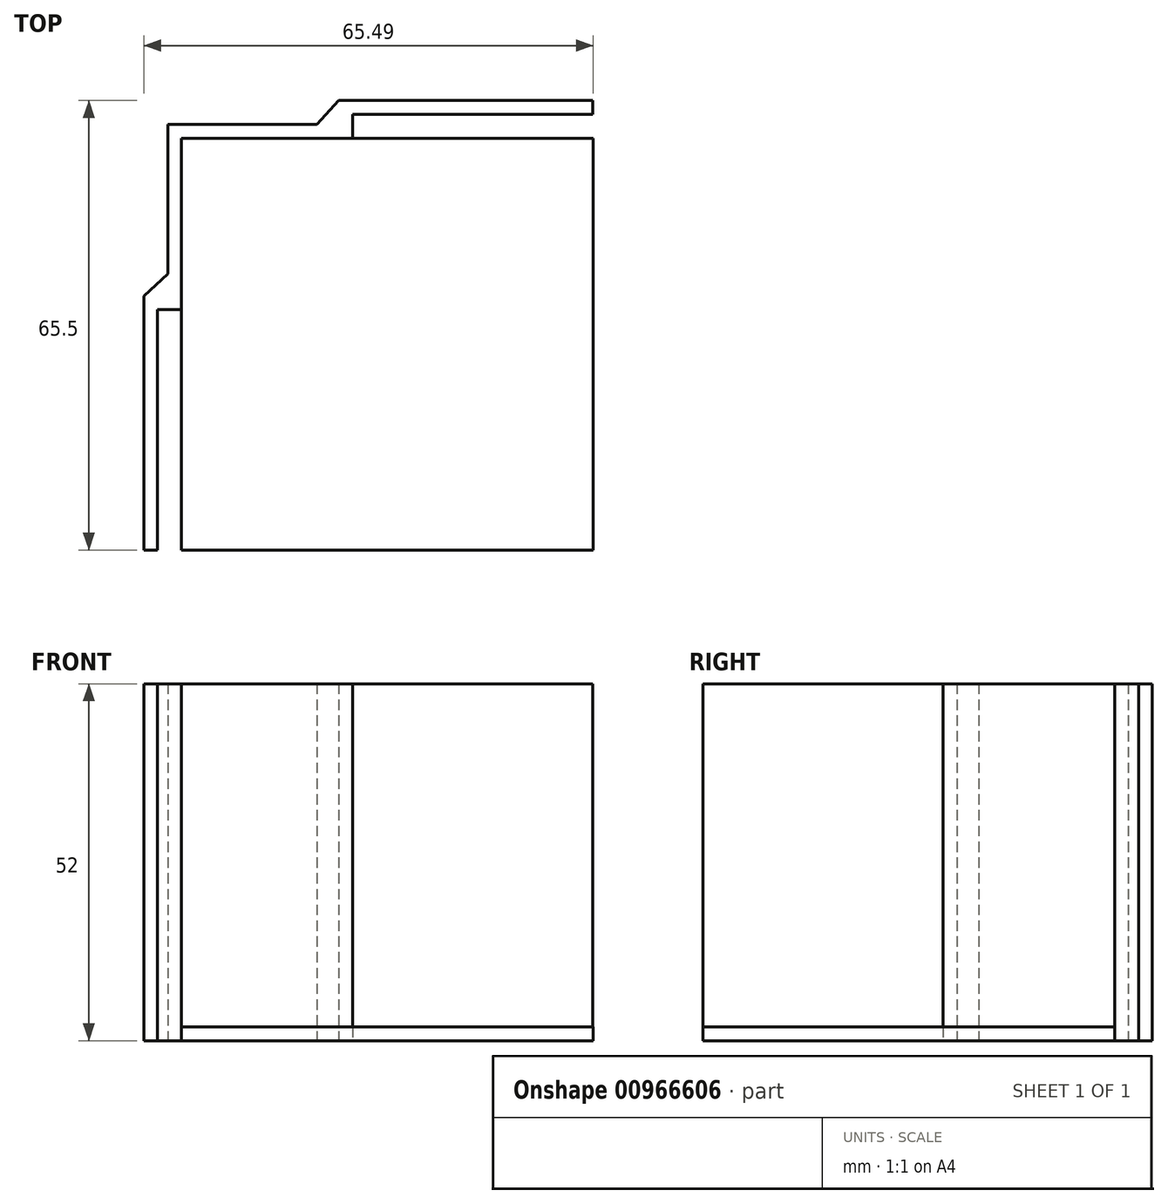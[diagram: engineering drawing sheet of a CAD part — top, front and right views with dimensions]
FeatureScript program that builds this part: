
annotation { "Feature Type Name" : "Feature", "Feature Type Description" : "" }
export const myFeature = defineFeature(function(context is Context, id is Id, definition is map)
    precondition{}
    {
        {
            var Q0;
            Q0=qCreatedBy(makeId("Top.planeOp"),FACE);
            var sketch = newSketch(context, id + "F0", { "sketchPlane" : qUnion([Q0])});
            skLineSegment(sketch, "E0.bottom", {"start": v(-29.86, 30.18) * mm, "end": v(30.14, 30.18) * mm});
            skLineSegment(sketch, "E0.top", {"start": v(-29.86, -29.82) * mm, "end": v(30.14, -29.82) * mm});
            skLineSegment(sketch, "E0.left", {"start": v(-29.86, 30.18) * mm, "end": v(-29.86, -29.82) * mm});
            skLineSegment(sketch, "E0.right", {"start": v(30.14, 30.18) * mm, "end": v(30.14, -29.82) * mm});
            skLineSegment(sketch, "E1", {"start": v(-29.86, 0.18) * mm, "end": v(30.14, 0.18) * mm});
            skLineSegment(sketch, "E2", {"start": v(0.14, 30.18) * mm, "end": v(0.14, -29.82) * mm});
            skLineSegment(sketch, "E3", {"start": v(-29.86, 30.18) * mm, "end": v(-29.86, 5.18) * mm});
            skLineSegment(sketch, "E4", {"start": v(-29.85, 5.18) * mm, "end": v(-33.35, 5.18) * mm});
            skLineSegment(sketch, "E5", {"start": v(-29.85, -29.82) * mm, "end": v(-33.35, -29.82) * mm});
            skLineSegment(sketch, "E6", {"start": v(-33.35, 5.18) * mm, "end": v(-33.35, -29.82) * mm});
            skLineSegment(sketch, "E7.1", {"start": v(-35.35, 7.18) * mm, "end": v(-35.35, -29.82) * mm});
            skLineSegment(sketch, "E7.2", {"start": v(-29.85, 7.18) * mm, "end": v(-35.35, 7.18) * mm});
            skLineSegment(sketch, "E8", {"start": v(-33.35, -29.82) * mm, "end": v(-35.35, -29.82) * mm});
            skLineSegment(sketch, "E9", {"start": v(-29.86, 30.18) * mm, "end": v(-4.86, 30.18) * mm});
            skLineSegment(sketch, "E10.MirrorCS", {"start": v(30.1, 30.18) * mm, "end": v(30.1, 33.68) * mm});
            skLineSegment(sketch, "E11.MirrorCS", {"start": v(-6.9, 30.18) * mm, "end": v(-6.9, 35.68) * mm});
            skLineSegment(sketch, "E12.MirrorCS", {"start": v(-6.9, 35.68) * mm, "end": v(30.1, 35.68) * mm});
            skLineSegment(sketch, "E13.MirrorCS", {"start": v(-4.9, 30.18) * mm, "end": v(-4.9, 33.68) * mm});
            skLineSegment(sketch, "E14.MirrorCS", {"start": v(-4.9, 33.68) * mm, "end": v(30.1, 33.68) * mm});
            skLineSegment(sketch, "E15.MirrorCS", {"start": v(30.1, 33.68) * mm, "end": v(30.1, 35.68) * mm});
            skLineSegment(sketch, "E16", {"start": v(-6.9, 30.18) * mm, "end": v(-11.93, 30.18) * mm});
            skLineSegment(sketch, "E17", {"start": v(-11.93, 30.18) * mm, "end": v(-6.9, 35.68) * mm});
            skLineSegment(sketch, "E18", {"start": v(-35.35, 7.18) * mm, "end": v(-29.86, 12.26) * mm});
            skLineSegment(sketch, "E19.0", {"start": v(-31.86, 32.18) * mm, "end": v(-4.86, 32.18) * mm});
            skLineSegment(sketch, "E19.1", {"start": v(-31.86, 32.18) * mm, "end": v(-31.86, 5.18) * mm});
            skSolve(sketch);
        }
        {
            var Q0;
            {var subQ0=sQuery(id+"F0.wireOp",EDGE,"E2");var subQ5=sQuery(id+"F0.wireOp",EDGE,"E0.bottom");var subQ8=makeQuery(id+"F0.imprint","INTERSECT",VERTEX,{"derivedFrom":[subQ5,subQ0]});Q0=makeQuery(id+"F0.imprint","IMPRINT",FACE,{"disambiguationData":[TD([[makeQuery(id+"F0.imprint","IMPRINT",EDGE,{"disambiguationData":[TD([[subQ8,-1.0]])],"derivedFrom":subQ5}),-1.0]])]});}
            var Q1;
            {var subQ0=sQuery(id+"F0.wireOp",EDGE,"E2");var subQ1=sQuery(id+"F0.wireOp",EDGE,"E0.top");var subQ2=makeQuery(id+"F0.imprint","INTERSECT",VERTEX,{"derivedFrom":[subQ1,subQ0]});Q1=makeQuery(id+"F0.imprint","IMPRINT",FACE,{"disambiguationData":[TD([[makeQuery(id+"F0.imprint","IMPRINT",EDGE,{"disambiguationData":[TD([[subQ2,-1.0]])],"derivedFrom":subQ1}),1.0]])]});}
            var Q2;
            {var subQ3=sQuery(id+"F0.wireOp",EDGE,"E0.top");var subQ5=makeQuery(id+"F0.imprint","IMPRINT",VERTEX,{"derivedFrom":subQ3});Q2=makeQuery(id+"F0.imprint","IMPRINT",FACE,{"disambiguationData":[TD([[makeQuery(id+"F0.imprint","IMPRINT",EDGE,{"disambiguationData":[TD([[subQ5,-1.0]])],"derivedFrom":subQ3}),1.0]])]});}
            var Q3;
            {var subQ6=sQuery(id+"F0.wireOp",EDGE,"E0.bottom");var subQ9=makeQuery(id+"F0.imprint","IMPRINT",VERTEX,{"derivedFrom":subQ6});Q3=makeQuery(id+"F0.imprint","IMPRINT",FACE,{"disambiguationData":[TD([[makeQuery(id+"F0.imprint","IMPRINT",EDGE,{"disambiguationData":[TD([[subQ9,-1.0]])],"derivedFrom":subQ6}),-1.0]])]});}
            extrude(context, id + "F1", {"entities" : qUnion([Q0, Q1, Q2, Q3]), "depth" : 2 * mm, "offsetDistance" : 25 * mm});
        }
        {
            var Q0;
            {var subQ4=sQuery(id+"F0.wireOp",EDGE,"E6");Q0=makeQuery(id+"F0.imprint","IMPRINT",FACE,{"disambiguationData":[TD([[makeQuery(id+"F0.imprint","IMPRINT",EDGE,{"derivedFrom":subQ4}),-1.0]])]});}
            var Q1;
            {var subQ0=sQuery(id+"F0.wireOp",EDGE,"E13.MirrorCS");var subQ1=sQuery(id+"F0.wireOp",EDGE,"E0.bottom");var subQ2=makeQuery(id+"F0.imprint","INTERSECT",VERTEX,{"derivedFrom":[subQ1,subQ0]});Q1=makeQuery(id+"F0.imprint","IMPRINT",FACE,{"disambiguationData":[TD([[makeQuery(id+"F0.imprint","IMPRINT",EDGE,{"disambiguationData":[TD([[subQ2,1.0]])],"derivedFrom":subQ1}),1.0]])]});}
            var Q2;
            {var subQ0=sQuery(id+"F0.wireOp",EDGE,"E19.0");var subQ1=sQuery(id+"F0.wireOp",EDGE,"E11.MirrorCS");var subQ2=makeQuery(id+"F0.imprint","INTERSECT",VERTEX,{"derivedFrom":[subQ1,subQ0]});Q2=makeQuery(id+"F0.imprint","IMPRINT",FACE,{"disambiguationData":[TD([[makeQuery(id+"F0.imprint","IMPRINT",EDGE,{"disambiguationData":[TD([[subQ2,1.0]])],"derivedFrom":subQ0}),1.0]])]});}
            var Q3;
            {var subQ1=sQuery(id+"F0.wireOp",EDGE,"E7.2");var subQ3=sQuery(id+"F0.wireOp",EDGE,"E19.1");var subQ4=makeQuery(id+"F0.imprint","INTERSECT",VERTEX,{"derivedFrom":[subQ1,subQ3]});Q3=makeQuery(id+"F0.imprint","IMPRINT",FACE,{"disambiguationData":[TD([[makeQuery(id+"F0.imprint","IMPRINT",EDGE,{"disambiguationData":[TD([[subQ4,1.0]])],"derivedFrom":subQ3}),-1.0]])]});}
            var Q4;
            {var subQ0=sQuery(id+"F0.wireOp",EDGE,"E17");var subQ1=sQuery(id+"F0.wireOp",EDGE,"E0.bottom");var subQ2=makeQuery(id+"F0.imprint","INTERSECT",VERTEX,{"derivedFrom":[subQ1,subQ0]});Q4=makeQuery(id+"F0.imprint","IMPRINT",FACE,{"disambiguationData":[TD([[makeQuery(id+"F0.imprint","IMPRINT",EDGE,{"disambiguationData":[TD([[subQ2,-1.0]])],"derivedFrom":subQ1}),1.0]])]});}
            var Q5;
            {var subQ4=sQuery(id+"F0.wireOp",EDGE,"E12.MirrorCS");Q5=makeQuery(id+"F0.imprint","IMPRINT",FACE,{"disambiguationData":[TD([[makeQuery(id+"F0.imprint","IMPRINT",EDGE,{"derivedFrom":subQ4}),-1.0]])]});}
            var Q6;
            {var subQ1=sQuery(id+"F0.wireOp",EDGE,"E0.left");var subQ8=sQuery(id+"F0.wireOp",EDGE,"E0.bottom");var subQ10=makeQuery(id+"F0.imprint","INTERSECT",VERTEX,{"derivedFrom":[subQ8,subQ1]});Q6=makeQuery(id+"F0.imprint","IMPRINT",FACE,{"disambiguationData":[TD([[makeQuery(id+"F0.imprint","IMPRINT",EDGE,{"disambiguationData":[TD([[subQ10,-1.0]])],"derivedFrom":subQ8}),1.0]])]});}
            var Q7;
            {var subQ0=sQuery(id+"F0.wireOp",EDGE,"E7.2");var subQ1=sQuery(id+"F0.wireOp",EDGE,"E0.left");var subQ2=makeQuery(id+"F0.imprint","INTERSECT",VERTEX,{"derivedFrom":[subQ1,subQ0]});Q7=makeQuery(id+"F0.imprint","IMPRINT",FACE,{"disambiguationData":[TD([[makeQuery(id+"F0.imprint","IMPRINT",EDGE,{"disambiguationData":[TD([[subQ2,1.0]])],"derivedFrom":subQ1}),-1.0]])]});}
            var Q8;
            {var subQ0=sQuery(id+"F0.wireOp",EDGE,"E4");var subQ1=sQuery(id+"F0.wireOp",EDGE,"E0.left");var subQ2=makeQuery(id+"F0.imprint","INTERSECT",VERTEX,{"derivedFrom":[subQ1,subQ0]});Q8=makeQuery(id+"F0.imprint","IMPRINT",FACE,{"disambiguationData":[TD([[makeQuery(id+"F0.imprint","IMPRINT",EDGE,{"disambiguationData":[TD([[subQ2,1.0]])],"derivedFrom":subQ1}),-1.0]])]});}
            extrude(context, id + "F2", {"entities" : qUnion([Q0, Q1, Q2, Q3, Q4, Q5, Q6, Q7, Q8]), "operationType" : NewBodyOperationType.ADD, "depth" : 52 * mm, "offsetDistance" : 25 * mm});
        }
    });
